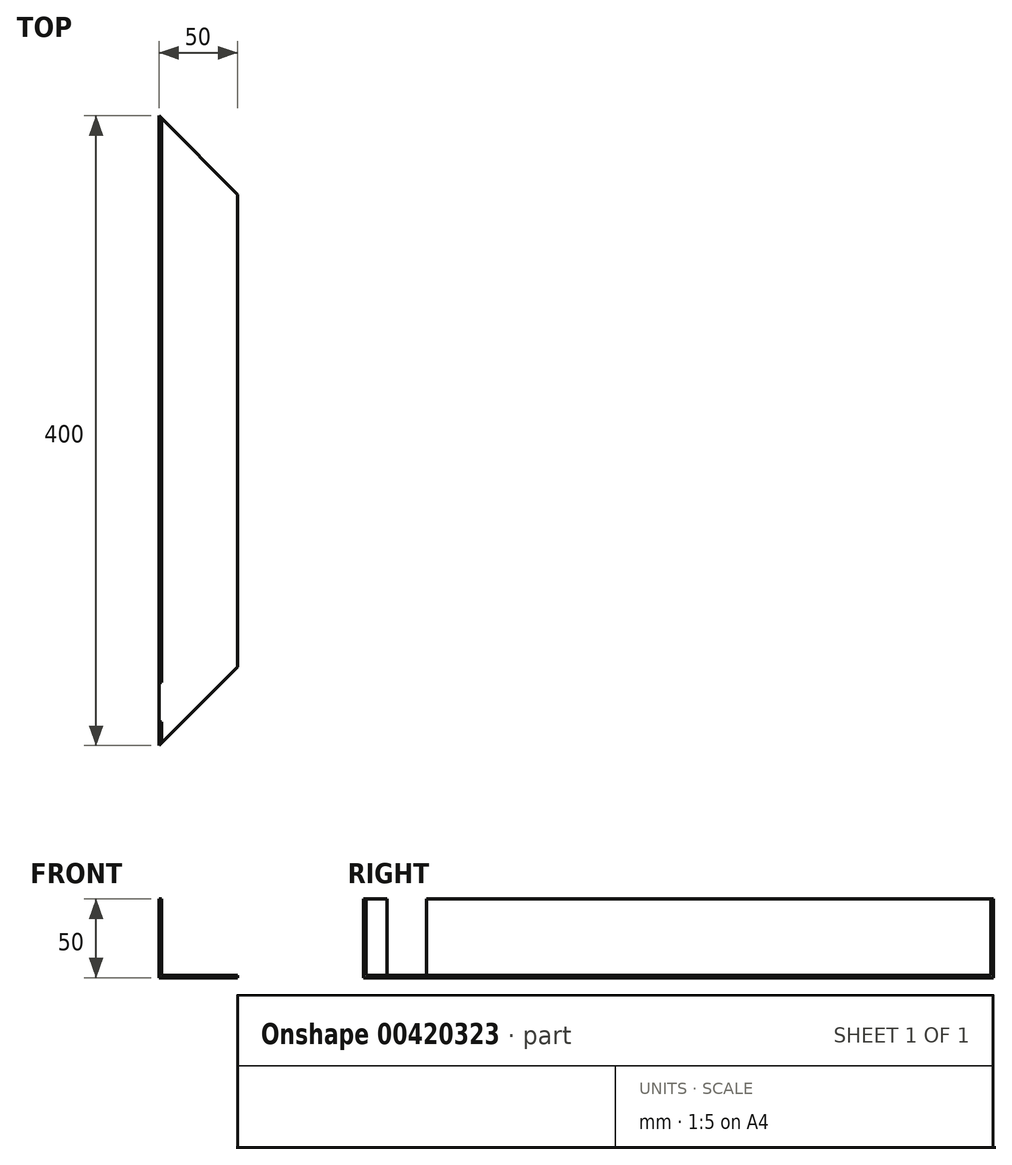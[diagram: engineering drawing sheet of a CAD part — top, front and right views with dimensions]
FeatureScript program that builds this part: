
annotation { "Feature Type Name" : "Feature", "Feature Type Description" : "" }
export const myFeature = defineFeature(function(context is Context, id is Id, definition is map)
    precondition{}
    {
        {
            var Q0;
            Q0=qCreatedBy(makeId("Front.planeOp"),FACE);
            var sketch = newSketch(context, id + "F0", { "sketchPlane" : qUnion([Q0])});
            skLineSegment(sketch, "E0.bottom", {"start": v(-33, 48.4) * mm, "end": v(-31.4, 48.4) * mm});
            skLineSegment(sketch, "E0.top", {"start": v(-33, -1.6) * mm, "end": v(-31.4, -1.6) * mm});
            skLineSegment(sketch, "E0.left", {"start": v(-33, 48.4) * mm, "end": v(-33, -1.6) * mm});
            skLineSegment(sketch, "E0.right", {"start": v(-31.4, 48.4) * mm, "end": v(-31.4, -1.6) * mm});
            skLineSegment(sketch, "E1.bottom", {"start": v(-33, -1.6) * mm, "end": v(17, -1.6) * mm});
            skLineSegment(sketch, "E1.top", {"start": v(-33, 0) * mm, "end": v(17, 0) * mm});
            skLineSegment(sketch, "E1.left", {"start": v(-33, -1.6) * mm, "end": v(-33, 0) * mm});
            skLineSegment(sketch, "E1.right", {"start": v(17, -1.6) * mm, "end": v(17, 0) * mm});
            skSolve(sketch);
        }
        {
            var Q0;
            Q0=qSketchRegion(id+"F0",true);
            extrude(context, id + "F1", {"entities" : qUnion([Q0]), "depth" : 400 * mm});
        }
        {
            var Q0;
            Q0=makeQuery(id+"F1.opExtrude","SWEPT_FACE",FACE,{"disambiguationData":[OSD([sQuery(id+"F0.wireOp",EDGE,"E1.bottom")])]});
            var sketch = newSketch(context, id + "F2", { "sketchPlane" : qUnion([Q0])});
            skLineSegment(sketch, "E2", {"start": v(-33, 0) * mm, "end": v(17, 50) * mm});
            skLineSegment(sketch, "E3", {"start": v(17, 50) * mm, "end": v(17, 0) * mm});
            skLineSegment(sketch, "E4", {"start": v(17, 0) * mm, "end": v(-33, 0) * mm});
            skSolve(sketch);
        }
        {
            var Q0;
            Q0=qSketchRegion(id+"F2",true);
            extrude(context, id + "F3", {"entities" : qUnion([Q0]), "operationType" : NewBodyOperationType.REMOVE, "endBound" : BoundingType.THROUGH_ALL, "oppositeDirection" : true, "depth" : 25 * mm});
        }
        {
            var Q0;
            Q0=makeQuery(id+"F1.opExtrude","SWEPT_FACE",FACE,{"disambiguationData":[OSD([sQuery(id+"F0.wireOp",EDGE,"E1.bottom")])]});
            var sketch = newSketch(context, id + "F4", { "sketchPlane" : qUnion([Q0])});
            skLineSegment(sketch, "E5", {"start": v(-33, 400) * mm, "end": v(17, 350) * mm});
            skLineSegment(sketch, "E6", {"start": v(17, 350) * mm, "end": v(17, 400) * mm});
            skLineSegment(sketch, "E7", {"start": v(17, 400) * mm, "end": v(-33, 400) * mm});
            skSolve(sketch);
        }
        {
            var Q0;
            Q0=qSketchRegion(id+"F4",true);
            extrude(context, id + "F5", {"entities" : qUnion([Q0]), "operationType" : NewBodyOperationType.REMOVE, "endBound" : BoundingType.THROUGH_ALL, "oppositeDirection" : true, "depth" : 25 * mm});
        }
        {
            var Q0;
            Q0=makeQuery(id+"F1.opExtrude","SWEPT_FACE",FACE,{"disambiguationData":[OSD([sQuery(id+"F0.wireOp",EDGE,"E0.left"),sQuery(id+"F0.wireOp",EDGE,"E1.left")])]});
            var sketch = newSketch(context, id + "F6", { "sketchPlane" : qUnion([Q0])});
            skLineSegment(sketch, "E8.bottom", {"start": v(385, 48.4) * mm, "end": v(360, 48.4) * mm});
            skLineSegment(sketch, "E9", {"start": v(360, 48.4) * mm, "end": v(360, 0) * mm});
            skLineSegment(sketch, "E10", {"start": v(385, 48.4) * mm, "end": v(385, 0) * mm});
            skLineSegment(sketch, "E11", {"start": v(385, 0) * mm, "end": v(360, 0) * mm});
            skSolve(sketch);
        }
        {
            var Q0;
            Q0=qSketchRegion(id+"F6",true);
            extrude(context, id + "F7", {"entities" : qUnion([Q0]), "operationType" : NewBodyOperationType.REMOVE, "endBound" : BoundingType.THROUGH_ALL, "oppositeDirection" : true, "depth" : 25 * mm});
        }
    });
